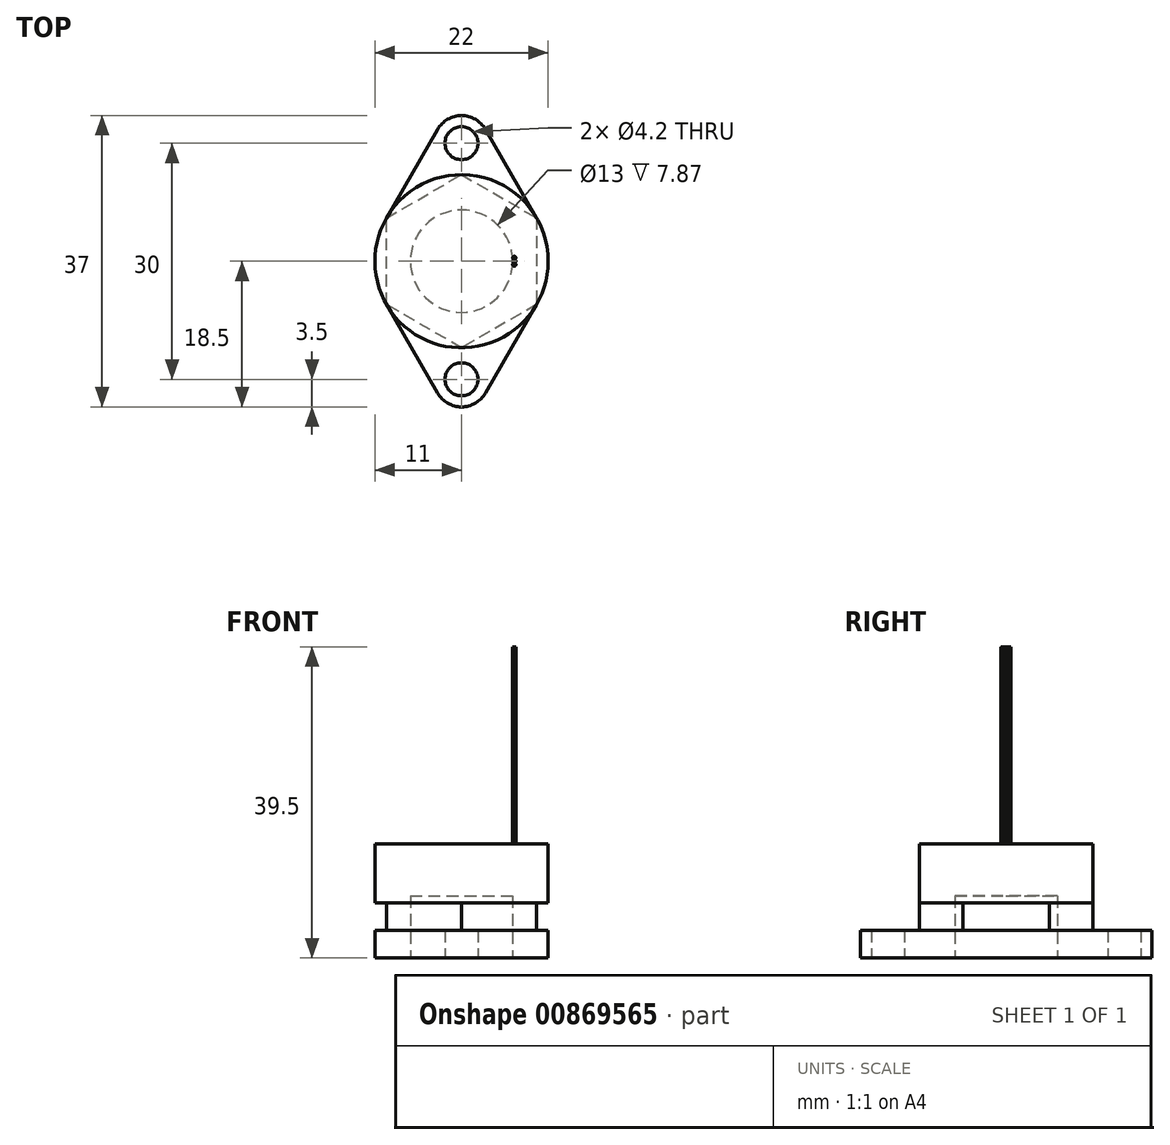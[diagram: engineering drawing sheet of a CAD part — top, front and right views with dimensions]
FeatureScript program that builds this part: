
annotation { "Feature Type Name" : "Feature", "Feature Type Description" : "" }
export const myFeature = defineFeature(function(context is Context, id is Id, definition is map)
    precondition{}
    {
        {
            var Q0;
            Q0=qCreatedBy(makeId("Top.planeOp"),FACE);
            var sketch = newSketch(context, id + "F0", { "sketchPlane" : qUnion([Q0])});
            skCircle(sketch, "E0", {"center": v(0, 0) * mm, "radius": 11 * mm});
            skSolve(sketch);
        }
        {
            var Q0;
            Q0 = qSketchRegion(id + "F0", true);
            extrude(context, id + "F1", {"entities" : qUnion([Q0]), "depth" : 14.5 * mm, "offsetDistance" : 25 * mm});
        }
        {
            var Q0;
            Q0=makeQuery(id+"F1.opExtrude","CAP_FACE",FACE,{"disambiguationData":[OSD([sQuery(id+"F0.wireOp",EDGE,"E0")])],"isStart":true});
            var sketch = newSketch(context, id + "F2", { "sketchPlane" : qUnion([Q0])});
            skCircle(sketch, "E1", {"center": v(0, 15) * mm, "radius": 2.1 * mm});
            skCircle(sketch, "E2", {"center": v(0, -15) * mm, "radius": 2.1 * mm});
            skLineSegment(sketch, "E3", {"start": v(0, -15) * mm, "end": v(0, 15) * mm, "construction": true});
            skPoint(sketch, "E4", {"position": v(0, 0) * mm});
            skArc(sketch, "E5", {"start": v(3.03, 16.75) * mm, "mid": v(0, 18.5) * mm, "end": v(-3.03, 16.75) * mm});
            skLineSegment(sketch, "E6", {"start": v(-3.03, 16.75) * mm, "end": v(-9.53, 5.5) * mm});
            skLineSegment(sketch, "E7", {"start": v(3.03, 16.75) * mm, "end": v(9.53, 5.5) * mm});
            skArc(sketch, "E8", {"start": v(-3.03, -16.75) * mm, "mid": v(0, -18.5) * mm, "end": v(3.03, -16.75) * mm});
            skLineSegment(sketch, "E9", {"start": v(3.03, -16.75) * mm, "end": v(9.53, -5.5) * mm});
            skLineSegment(sketch, "E10", {"start": v(-3.03, -16.75) * mm, "end": v(-9.53, -5.5) * mm});
            skArc(sketch, "E11", {"start": v(-9.53, 5.5) * mm, "mid": v(-11, 0) * mm, "end": v(-9.53, -5.5) * mm});
            skArc(sketch, "E12.trimOffspring", {"start": v(9.53, -5.5) * mm, "mid": v(11, 0) * mm, "end": v(9.53, 5.5) * mm});
            skSolve(sketch);
        }
        {
            var Q0;
            Q0 = qSketchRegion(id + "F2", true);
            extrude(context, id + "F3", {"entities" : qUnion([Q0]), "operationType" : NewBodyOperationType.ADD, "oppositeDirection" : true, "depth" : 3.5 * mm, "offsetDistance" : 25 * mm});
        }
        {
            var Q0;
            {var subQ0=sQuery(id+"F2.wireOp",EDGE,"E9");var subQ1=sQuery(id+"F2.wireOp",EDGE,"E2");var subQ2=sQuery(id+"F2.wireOp",EDGE,"E8");var subQ3=sQuery(id+"F2.wireOp",EDGE,"E10");Q0=makeQuery(id+"F3.boolean.opBoolean","SPLIT",FACE,{"disambiguationData":[TD([makeQuery(id+"F3.opExtrude","SWEPT_FACE",FACE,{"disambiguationData":[OSD([subQ1])]})])],"derivedFrom":makeQuery(id+"F3.opExtrude","CAP_FACE",FACE,{"disambiguationData":[OSD([sQuery(id+"F2.wireOp",EDGE,"E1"),sQuery(id+"F2.wireOp",EDGE,"E5"),subQ1,sQuery(id+"F2.wireOp",EDGE,"E6"),sQuery(id+"F2.wireOp",EDGE,"E7"),subQ2,subQ0,subQ3,sQuery(id+"F2.wireOp",EDGE,"E11"),sQuery(id+"F2.wireOp",EDGE,"E12.trimOffspring")])],"isStart":false})});}
            var sketch = newSketch(context, id + "F4", { "sketchPlane" : qUnion([Q0])});
            skCircle(sketch, "E13", {"center": v(0, 0) * mm, "radius": 11 * mm});
            skSolve(sketch);
        }
        {
            var Q0;
            Q0 = qSketchRegion(id + "F4", true);
            extrude(context, id + "F5", {"entities" : qUnion([Q0]), "operationType" : NewBodyOperationType.REMOVE, "depth" : 3.5 * mm, "offsetDistance" : 25 * mm});
        }
        {
            var Q0;
            {var subQ0=sQuery(id+"F2.wireOp",EDGE,"E9");var subQ1=sQuery(id+"F2.wireOp",EDGE,"E2");var subQ2=sQuery(id+"F2.wireOp",EDGE,"E8");var subQ4=sQuery(id+"F2.wireOp",EDGE,"E10");var subQ5=sQuery(id+"F2.wireOp",EDGE,"E7");var subQ6=sQuery(id+"F2.wireOp",EDGE,"E6");var subQ7=sQuery(id+"F2.wireOp",EDGE,"E5");var subQ8=sQuery(id+"F2.wireOp",EDGE,"E1");var subQ9=makeQuery(id+"F3.opExtrude","CAP_FACE",FACE,{"disambiguationData":[OSD([subQ8,subQ7,subQ1,subQ6,subQ5,subQ2,subQ0,subQ4,sQuery(id+"F2.wireOp",EDGE,"E11"),sQuery(id+"F2.wireOp",EDGE,"E12.trimOffspring")])],"isStart":false});Q0=makeQuery(id+"F5.boolean.opBoolean","MERGE",FACE,{"derivedFrom":[makeQuery(id+"F3.boolean.opBoolean","SPLIT",FACE,{"disambiguationData":[TD([makeQuery(id+"F3.opExtrude","SWEPT_FACE",FACE,{"disambiguationData":[OSD([subQ8])]})])],"derivedFrom":subQ9}),makeQuery(id+"F3.boolean.opBoolean","SPLIT",FACE,{"disambiguationData":[TD([makeQuery(id+"F3.opExtrude","SWEPT_FACE",FACE,{"disambiguationData":[OSD([subQ1])]})])],"derivedFrom":subQ9})],"fromTools":[makeQuery(id+"F5.opExtrude","CAP_FACE",FACE,{"disambiguationData":[OSD([sQuery(id+"F4.wireOp",EDGE,"E13")])],"isStart":true})]});}
            var sketch = newSketch(context, id + "F6", { "sketchPlane" : qUnion([Q0])});
            skCircle(sketch, "E14.cCircle", {"center": v(0, 0) * mm, "radius": 11 * mm, "construction": true});
            skLineSegment(sketch, "E14.0", {"start": v(0, 11) * mm, "end": v(9.53, 5.5) * mm});
            skLineSegment(sketch, "E14.1", {"start": v(9.53, 5.5) * mm, "end": v(9.53, -5.5) * mm});
            skLineSegment(sketch, "E14.2", {"start": v(9.53, -5.5) * mm, "end": v(0, -11) * mm});
            skLineSegment(sketch, "E14.3", {"start": v(0, -11) * mm, "end": v(-9.53, -5.5) * mm});
            skLineSegment(sketch, "E14.4", {"start": v(-9.53, -5.5) * mm, "end": v(-9.53, 5.5) * mm});
            skLineSegment(sketch, "E14.5", {"start": v(-9.53, 5.5) * mm, "end": v(0, 11) * mm});
            skSolve(sketch);
        }
        {
            var Q0;
            Q0 = qSketchRegion(id + "F6", true);
            extrude(context, id + "F7", {"entities" : qUnion([Q0]), "operationType" : NewBodyOperationType.ADD, "depth" : 3.5 * mm, "offsetDistance" : 25 * mm});
        }
        {
            var Q0;
            Q0=makeQuery(id+"F3.boolean.opBoolean","MERGE",FACE,{"derivedFrom":[makeQuery(id+"F1.opExtrude","CAP_FACE",FACE,{"disambiguationData":[OSD([sQuery(id+"F0.wireOp",EDGE,"E0")])],"isStart":true}),makeQuery(id+"F3.opExtrude","CAP_FACE",FACE,{"disambiguationData":[OSD([sQuery(id+"F2.wireOp",EDGE,"E1"),sQuery(id+"F2.wireOp",EDGE,"E5"),sQuery(id+"F2.wireOp",EDGE,"E2"),sQuery(id+"F2.wireOp",EDGE,"E6"),sQuery(id+"F2.wireOp",EDGE,"E7"),sQuery(id+"F2.wireOp",EDGE,"E8"),sQuery(id+"F2.wireOp",EDGE,"E9"),sQuery(id+"F2.wireOp",EDGE,"E10"),sQuery(id+"F2.wireOp",EDGE,"E11"),sQuery(id+"F2.wireOp",EDGE,"E12.trimOffspring")])],"isStart":true})]});
            var sketch = newSketch(context, id + "F8", { "sketchPlane" : qUnion([Q0])});
            skCircle(sketch, "E15", {"center": v(0, 0) * mm, "radius": 6.5 * mm});
            skSolve(sketch);
        }
        {
            var Q0;
            Q0 = qSketchRegion(id + "F8", true);
            extrude(context, id + "F9", {"entities" : qUnion([Q0]), "operationType" : NewBodyOperationType.REMOVE, "flatOperationType" : FlatOperationType.REMOVE, "oppositeDirection" : true, "depth" : 7.87 * mm, "offsetDistance" : 25 * mm, "domain" : OperationDomain.MODEL});
        }
        {
            var Q0;
            Q0=makeQuery(id+"F1.opExtrude","CAP_FACE",FACE,{"disambiguationData":[OSD([sQuery(id+"F0.wireOp",EDGE,"E0")])],"isStart":false});
            var sketch = newSketch(context, id + "F10", { "sketchPlane" : qUnion([Q0])});
            skCircle(sketch, "E16", {"center": v(6.7, 0) * mm, "radius": 0.2 * mm});
            skCircle(sketch, "E17", {"center": v(6.7, 0.43) * mm, "radius": 0.2 * mm});
            skCircle(sketch, "E18", {"center": v(6.7, -0.43) * mm, "radius": 0.2 * mm});
            skSolve(sketch);
        }
        {
            var Q0;
            Q0 = qSketchRegion(id + "F10", true);
            extrude(context, id + "F11", {"entities" : qUnion([Q0]), "operationType" : NewBodyOperationType.ADD, "depth" : 25 * mm, "offsetDistance" : 25 * mm});
        }
    });
